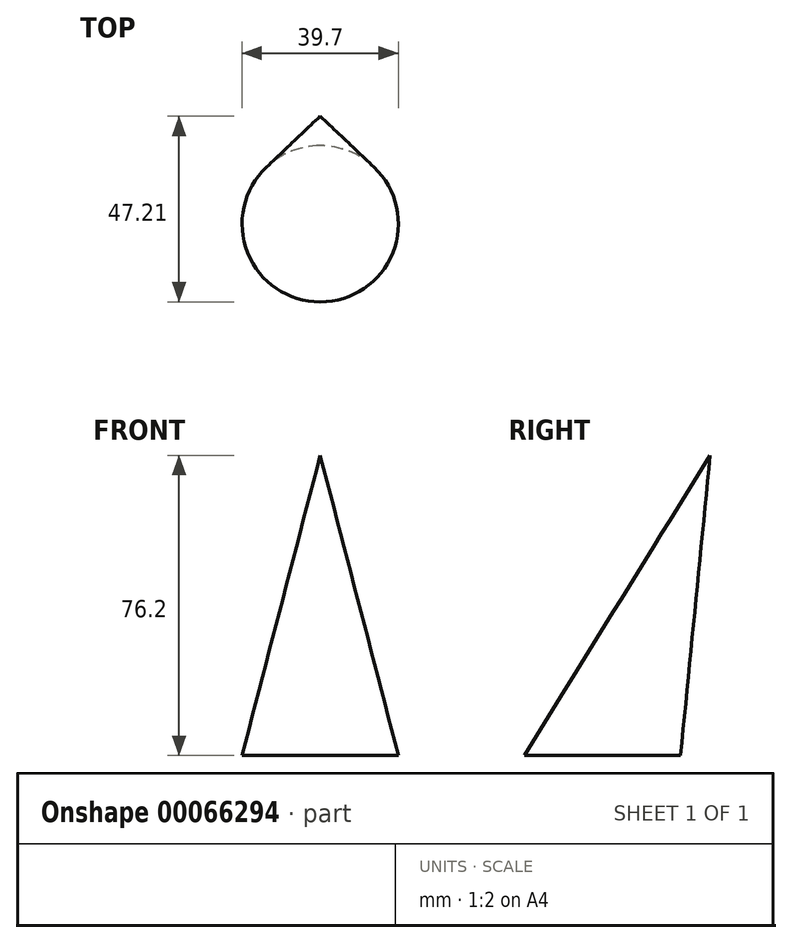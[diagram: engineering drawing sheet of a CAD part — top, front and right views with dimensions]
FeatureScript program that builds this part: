
annotation { "Feature Type Name" : "Feature", "Feature Type Description" : "" }
export const myFeature = defineFeature(function(context is Context, id is Id, definition is map)
    precondition{}
    {
        {
            var Q0;
            Q0=qCreatedBy(makeId("Top.planeOp"),FACE);
            var sketch = newSketch(context, id + "F0", { "sketchPlane" : qUnion([Q0])});
            skCircle(sketch, "E0", {"center": v(0, 0) * mm, "radius": 19.85 * mm});
            skSolve(sketch);
        }
        {
            var Q0;
            Q0=qCreatedBy(makeId("Top.planeOp"),FACE);
            cPlane(context, id + "F1", {"entities" : qUnion([Q0]), "cplaneType" : CPlaneType.OFFSET, "offset" : 76.2 * mm, "width" : 152.4 * mm, "height" : 152.4 * mm});
        }
        {
            var Q0;
            Q0=qCreatedBy(id+"F1.planeOp",FACE);
            var sketch = newSketch(context, id + "F2", { "sketchPlane" : qUnion([Q0])});
            skPoint(sketch, "E1", {"position": v(0, 27.36) * mm});
            skSolve(sketch);
        }
        {
            var Q0;
            Q0=sQuery(id+"F2.wireOp",VERTEX,"E1");
            var Q1;
            Q1=makeQuery(id+"F0.imprint","IMPRINT",FACE,{"disambiguationData":[TD([[makeQuery(id+"F0.imprint","IMPRINT",EDGE,{"derivedFrom":sQuery(id+"F0.wireOp",EDGE,"E0")}),1.0]])]});
            var Q2;
            Q2 = qConstructionFilter(qBodyType(qCreatedBy(id + "Fo0ySX0NyckAbSc_1" ,EDGE), BodyType.WIRE), ConstructionObject.NO);
            loft(context, id + "F3", {"addGuides" : true, "sheetProfilesArray" : [{ "sheetProfileEntities" : qUnion([Q0]) }, { "sheetProfileEntities" : qUnion([Q1]) }], "guidesArray" : [{ "guideEntities" : qUnion([Q2]), "guideDerivativeType" : LoftGuideDerivativeType.DEFAULT, "guideDerivativeMagnitude" : 1 }]});
        }
    });
